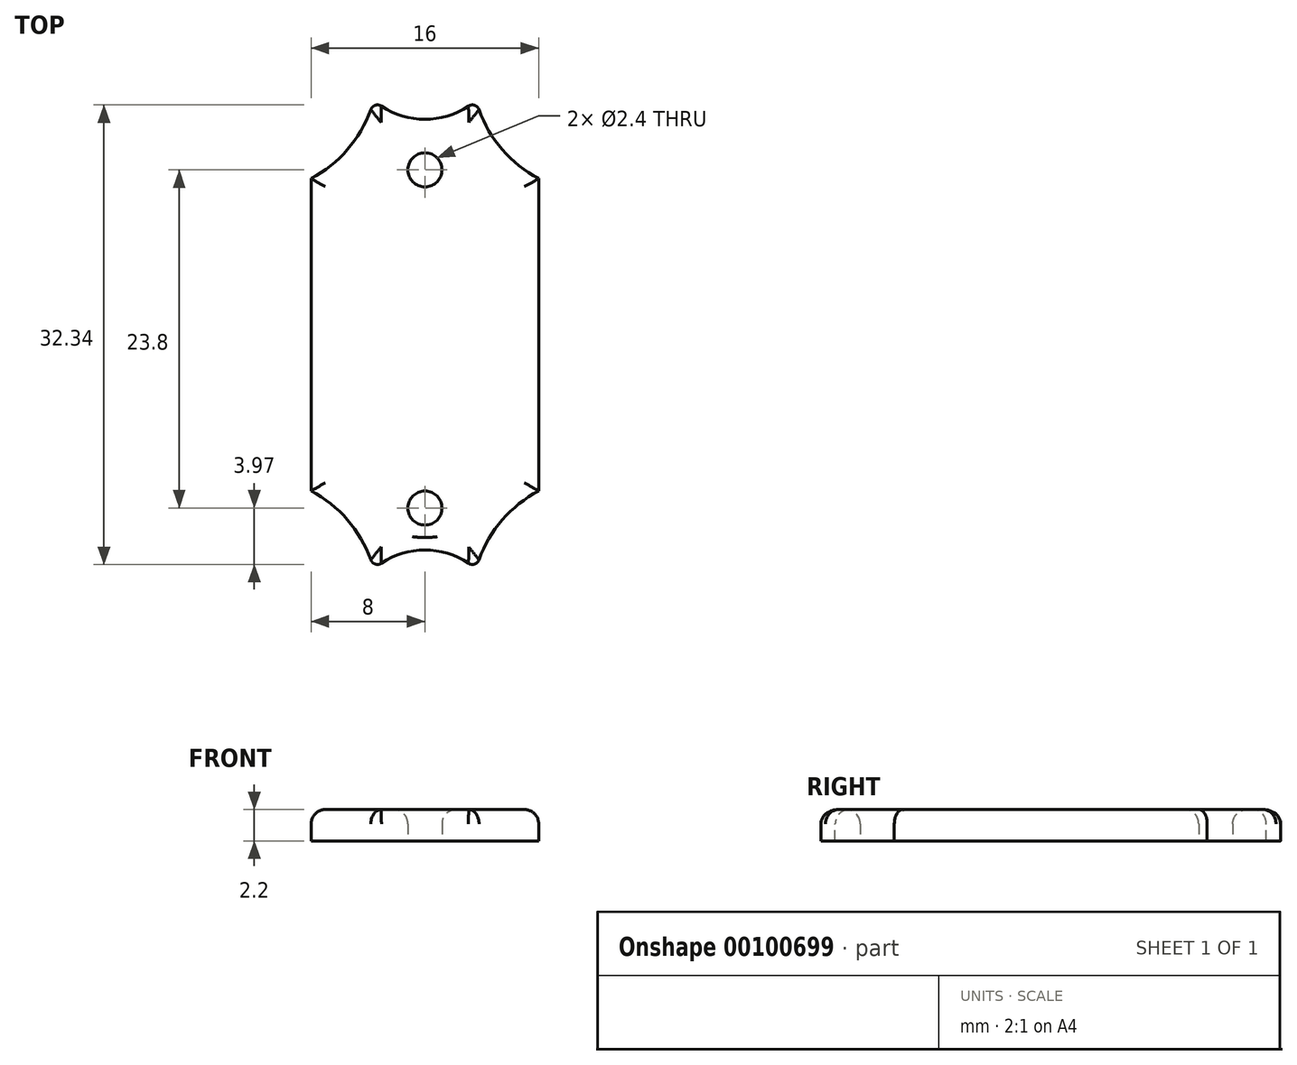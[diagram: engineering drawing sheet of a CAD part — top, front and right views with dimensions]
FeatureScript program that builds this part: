
annotation { "Feature Type Name" : "Feature", "Feature Type Description" : "" }
export const myFeature = defineFeature(function(context is Context, id is Id, definition is map)
    precondition{}
    {
        {
            var Q0;
            Q0=qCreatedBy(makeId("Top.planeOp"),FACE);
            var sketch = newSketch(context, id + "F0", { "sketchPlane" : qUnion([Q0])});
            skLineSegment(sketch, "E0.bottom", {"start": v(8, -16.5) * mm, "end": v(-8, -16.5) * mm});
            skLineSegment(sketch, "E0.top", {"start": v(8, 16.5) * mm, "end": v(-8, 16.5) * mm});
            skLineSegment(sketch, "E0.left", {"start": v(8, -16.5) * mm, "end": v(8, 16.5) * mm});
            skLineSegment(sketch, "E0.right", {"start": v(-8, -16.5) * mm, "end": v(-8, 16.5) * mm});
            skPoint(sketch, "E0.middle", {"position": v(0, 0) * mm});
            skSolve(sketch);
        }
        {
            var Q0;
            Q0=qSketchRegion(id+"F0",true);
            extrude(context, id + "F3", {"entities" : qUnion([Q0]), "depth" : 2.2 * mm});
        }
        {
            var Q0;
            Q0=makeQuery(id+"F3.opExtrude","CAP_FACE",FACE,{"disambiguationData":[OSD([sQuery(id+"F0.wireOp",EDGE,"E0.bottom"),sQuery(id+"F0.wireOp",EDGE,"E0.top"),sQuery(id+"F0.wireOp",EDGE,"E0.left"),sQuery(id+"F0.wireOp",EDGE,"E0.right")])],"isStart":false});
            var sketch = newSketch(context, id + "F1", { "sketchPlane" : qUnion([Q0])});
            skLineSegment(sketch, "E1", {"start": v(8, -16.5) * mm, "end": v(8, -11) * mm, "construction": true});
            skLineSegment(sketch, "E2", {"start": v(8, -16.5) * mm, "end": v(3.6, -16.5) * mm, "construction": true});
            skLineSegment(sketch, "E3", {"start": v(3.6, -16.5) * mm, "end": v(3.6, -11) * mm, "construction": true});
            skLineSegment(sketch, "E4", {"start": v(8, -11) * mm, "end": v(3.6, -11) * mm, "construction": true});
            skPoint(sketch, "E5.orphan", {"position": v(0, -11) * mm});
            skArc(sketch, "E6", {"start": v(8, -11) * mm, "mid": v(5.23, -13.3) * mm, "end": v(3.6, -16.5) * mm});
            skLineSegment(sketch, "E7", {"start": v(0, -16.5) * mm, "end": v(0, 0) * mm, "construction": true});
            skLineSegment(sketch, "E8.MirrorCS", {"start": v(-3.6, -16.5) * mm, "end": v(-3.6, -11) * mm, "construction": true});
            skLineSegment(sketch, "E9.MirrorCS", {"start": v(-8, -11) * mm, "end": v(-3.6, -11) * mm, "construction": true});
            skArc(sketch, "E10.MirrorC", {"start": v(-8, -11) * mm, "mid": v(-5.23, -13.3) * mm, "end": v(-3.6, -16.5) * mm});
            skArc(sketch, "E11", {"start": v(3.6, -16.5) * mm, "mid": v(0, -15.16) * mm, "end": v(-3.6, -16.5) * mm});
            skLineSegment(sketch, "E12", {"start": v(-8, 0) * mm, "end": v(8, 0) * mm, "construction": true});
            skArc(sketch, "E13.MirrorCS", {"start": v(-8, 11) * mm, "mid": v(-5.23, 13.3) * mm, "end": v(-3.6, 16.5) * mm});
            skArc(sketch, "E14.MirrorCS", {"start": v(3.6, 16.5) * mm, "mid": v(0, 15.16) * mm, "end": v(-3.6, 16.5) * mm});
            skArc(sketch, "E15.MirrorCS", {"start": v(8, 11) * mm, "mid": v(5.23, 13.3) * mm, "end": v(3.6, 16.5) * mm});
            skLineSegment(sketch, "E16", {"start": v(-8, -11) * mm, "end": v(-8, -33.11) * mm});
            skLineSegment(sketch, "E17.MirrorCS", {"start": v(8, -11) * mm, "end": v(8, -33.11) * mm});
            skLineSegment(sketch, "E18.MirrorCS", {"start": v(-8, 11) * mm, "end": v(-8, 33.11) * mm});
            skLineSegment(sketch, "E19.MirrorCS", {"start": v(8, 11) * mm, "end": v(8, 33.11) * mm});
            skLineSegment(sketch, "E20", {"start": v(-8, 33.11) * mm, "end": v(8, 33.11) * mm});
            skLineSegment(sketch, "E21", {"start": v(-8, -33.11) * mm, "end": v(8, -33.11) * mm});
            skSolve(sketch);
        }
        {
            var Q0;
            Q0 = qSketchRegion(id + "F1", true);
            extrude(context, id + "F4", {"entities" : qUnion([Q0]), "operationType" : NewBodyOperationType.REMOVE, "oppositeDirection" : true, "depth" : 25 * mm});
        }
        {
            var Q0;
            Q0=makeQuery(id+"F4.boolean.opBoolean","COPY",EDGE,{"derivedFrom":makeQuery(id+"F4.opExtrude","SWEPT_EDGE",EDGE,{"disambiguationData":[OSD([sQuery(id+"F0.wireOp",EDGE,"E0.right"),sQuery(id+"F1.wireOp",EDGE,"E10.MirrorC"),sQuery(id+"F1.wireOp",EDGE,"E16")])]})});
            var Q1;
            Q1=makeQuery(id+"F4.boolean.opBoolean","COPY",EDGE,{"derivedFrom":makeQuery(id+"F4.opExtrude","SWEPT_EDGE",EDGE,{"disambiguationData":[OSD([sQuery(id+"F0.wireOp",EDGE,"E0.bottom"),sQuery(id+"F1.wireOp",EDGE,"E10.MirrorC"),sQuery(id+"F1.wireOp",EDGE,"E11")])]})});
            var Q2;
            Q2=makeQuery(id+"F4.boolean.opBoolean","COPY",EDGE,{"derivedFrom":makeQuery(id+"F4.opExtrude","SWEPT_EDGE",EDGE,{"disambiguationData":[OSD([sQuery(id+"F0.wireOp",EDGE,"E0.bottom"),sQuery(id+"F1.wireOp",EDGE,"E6"),sQuery(id+"F1.wireOp",EDGE,"E11")])]})});
            var Q3;
            Q3=makeQuery(id+"F4.boolean.opBoolean","COPY",EDGE,{"derivedFrom":makeQuery(id+"F4.opExtrude","SWEPT_EDGE",EDGE,{"disambiguationData":[OSD([sQuery(id+"F0.wireOp",EDGE,"E0.left"),sQuery(id+"F1.wireOp",EDGE,"E6"),sQuery(id+"F1.wireOp",EDGE,"E17.MirrorCS")])]})});
            var Q4;
            Q4=makeQuery(id+"F4.boolean.opBoolean","COPY",EDGE,{"derivedFrom":makeQuery(id+"F4.opExtrude","SWEPT_EDGE",EDGE,{"disambiguationData":[OSD([sQuery(id+"F0.wireOp",EDGE,"E0.left"),sQuery(id+"F1.wireOp",EDGE,"E15.MirrorCS"),sQuery(id+"F1.wireOp",EDGE,"E19.MirrorCS")])]})});
            var Q5;
            Q5=makeQuery(id+"F4.boolean.opBoolean","COPY",EDGE,{"derivedFrom":makeQuery(id+"F4.opExtrude","SWEPT_EDGE",EDGE,{"disambiguationData":[OSD([sQuery(id+"F0.wireOp",EDGE,"E0.top"),sQuery(id+"F1.wireOp",EDGE,"E14.MirrorCS"),sQuery(id+"F1.wireOp",EDGE,"E15.MirrorCS")])]})});
            var Q6;
            Q6=makeQuery(id+"F4.boolean.opBoolean","COPY",EDGE,{"derivedFrom":makeQuery(id+"F4.opExtrude","SWEPT_EDGE",EDGE,{"disambiguationData":[OSD([sQuery(id+"F0.wireOp",EDGE,"E0.top"),sQuery(id+"F1.wireOp",EDGE,"E13.MirrorCS"),sQuery(id+"F1.wireOp",EDGE,"E14.MirrorCS")])]})});
            var Q7;
            Q7=makeQuery(id+"F4.boolean.opBoolean","COPY",EDGE,{"derivedFrom":makeQuery(id+"F4.opExtrude","SWEPT_EDGE",EDGE,{"disambiguationData":[OSD([sQuery(id+"F0.wireOp",EDGE,"E0.right"),sQuery(id+"F1.wireOp",EDGE,"E13.MirrorCS"),sQuery(id+"F1.wireOp",EDGE,"E18.MirrorCS")])]})});
            fillet(context, id + "F5", {"entities" : qUnion([Q0, Q1, Q2, Q3, Q4, Q5, Q6, Q7]), "radius" : 0.5 * mm, "tangentPropagation" : true, "allowEdgeOverflow" : false});
        }
        {
            var Q0;
            Q0=makeQuery(id+"F3.opExtrude","CAP_FACE",FACE,{"disambiguationData":[OSD([sQuery(id+"F0.wireOp",EDGE,"E0.bottom"),sQuery(id+"F0.wireOp",EDGE,"E0.top"),sQuery(id+"F0.wireOp",EDGE,"E0.left"),sQuery(id+"F0.wireOp",EDGE,"E0.right")])],"isStart":false});
            var sketch = newSketch(context, id + "F2", { "sketchPlane" : qUnion([Q0])});
            skLineSegment(sketch, "E22", {"start": v(0, 0) * mm, "end": v(0, -2.2) * mm, "construction": true});
            skCircle(sketch, "E23", {"center": v(0, -2.2) * mm, "radius": 3.3 * mm, "construction": true});
            skLineSegment(sketch, "E24", {"start": v(0, -2.2) * mm, "end": v(0, -12.2) * mm, "construction": true});
            skLineSegment(sketch, "E25", {"start": v(0, -2.2) * mm, "end": v(0, 11.6) * mm, "construction": true});
            skPoint(sketch, "E26", {"position": v(0, 11.6) * mm});
            skPoint(sketch, "E27", {"position": v(0, -12.2) * mm});
            skSolve(sketch);
        }
        {
            var Q0;
            Q0=sQuery(id+"F2.wireOp",VERTEX,"E26");
            var Q1;
            Q1=sQuery(id+"F2.wireOp",VERTEX,"E27");
            var Q2;
            Q2=makeQuery(id+"F3.opExtrude","SWEPT_BODY",BODY,{"disambiguationData":[OSD([sQuery(id+"F0.wireOp",EDGE,"E0.bottom"),sQuery(id+"F0.wireOp",EDGE,"E0.top"),sQuery(id+"F0.wireOp",EDGE,"E0.left"),sQuery(id+"F0.wireOp",EDGE,"E0.right")])]});
            hole(context, id + "F6", {"style" : HoleStyle.SIMPLE, "endStyle" : HoleEndStyle.THROUGH, "holeDiameter" : 2.4 * mm, "locations" : qUnion([Q0, Q1]), "scope" : qUnion([Q2]), "isTappedThrough" : true, "startStyle" : HoleStartStyle.PART});
        }
        {
            var Q0;
            Q0=makeQuery(id+"F3.opExtrude","CAP_FACE",FACE,{"disambiguationData":[OSD([sQuery(id+"F0.wireOp",EDGE,"E0.bottom"),sQuery(id+"F0.wireOp",EDGE,"E0.top"),sQuery(id+"F0.wireOp",EDGE,"E0.left"),sQuery(id+"F0.wireOp",EDGE,"E0.right")])],"isStart":false});
            fillet(context, id + "F7", {"entities" : qUnion([Q0]), "radius" : 1 * mm, "tangentPropagation" : true, "allowEdgeOverflow" : false});
        }
    });
